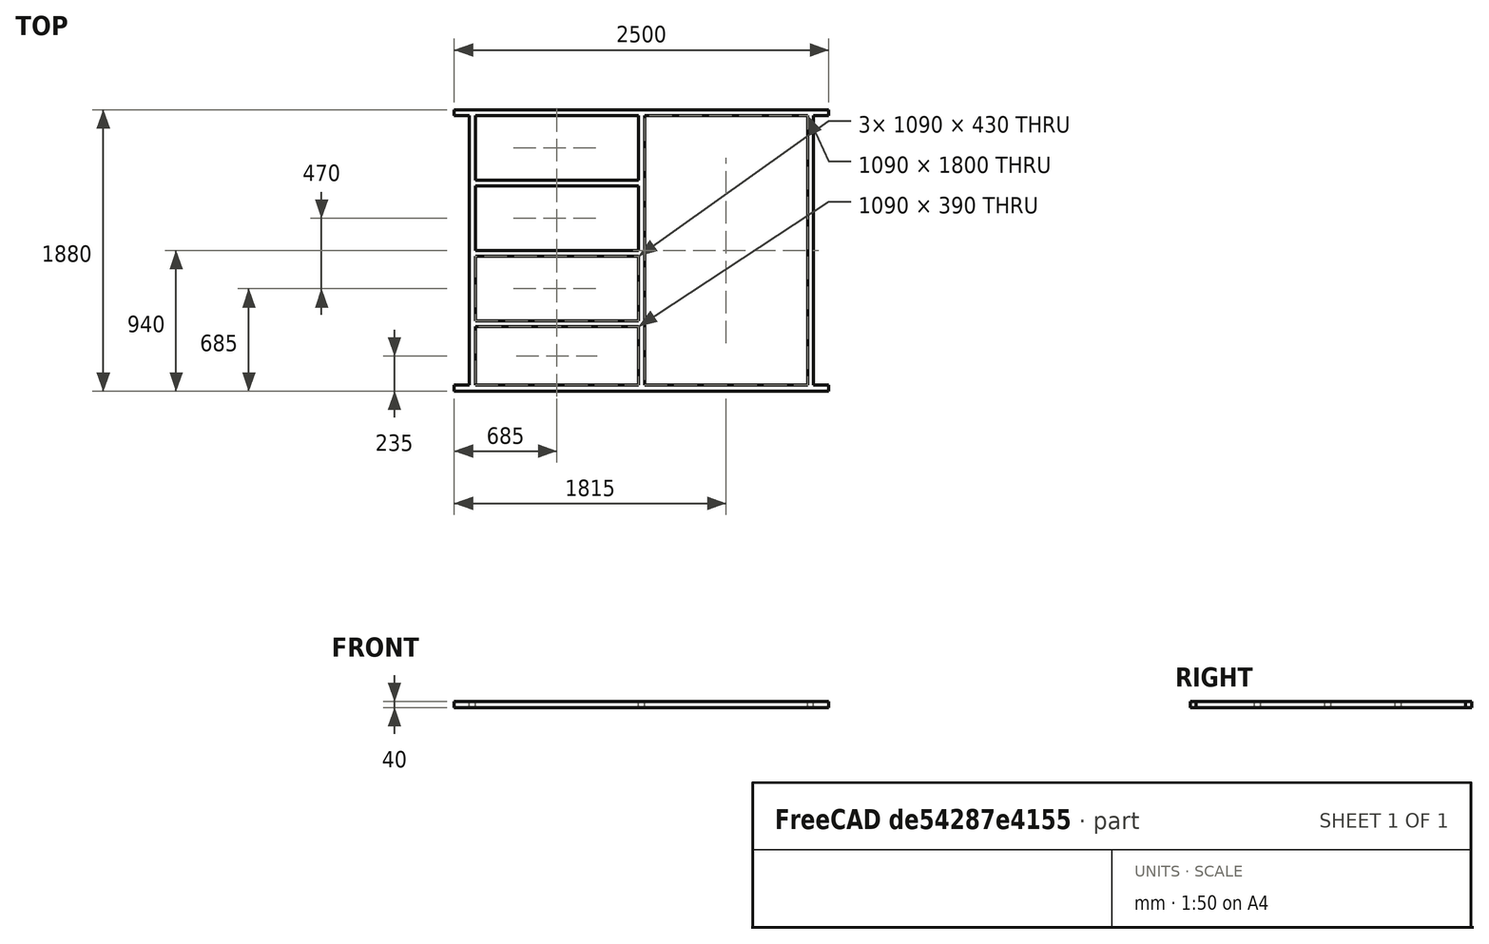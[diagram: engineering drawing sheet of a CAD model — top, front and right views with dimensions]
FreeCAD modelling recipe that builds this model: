
FCSTD DOCUMENT  (FreeCAD 0.19R24291 (Git))
Label: planche jacuzzy
License: All rights reserved
LicenseURL: http://en.wikipedia.org/wiki/All_rights_reserved
objects: Sketcher::SketchObject×1, PartDesign::Pad×1, PartDesign::Body×1
note: 4 computed .brp shape members not serialized (recipe doc carries the construction recipe); baked Part::Feature solids carry a one-line shape summary decoded from their .brp

FEATURE [Sketcher::SketchObject] Sketch
  FullyConstrained = true
  MapMode = 5
  Support = -> [XY_Plane]
  sketch-geometry (32):
    g0: LineSegment StartX=-1250 StartY=940 StartZ=0 EndX=1250 EndY=940 EndZ=0
    g1: LineSegment StartX=1250 StartY=-940 StartZ=0 EndX=-1250 EndY=-940 EndZ=0
    g2: LineSegment StartX=-1250 StartY=900 StartZ=0 EndX=-1150 EndY=900 EndZ=0
    g3: LineSegment StartX=1250 StartY=-900 StartZ=0 EndX=1150 EndY=-900 EndZ=0
    g4: LineSegment StartX=-1250 StartY=940 StartZ=0 EndX=-1250 EndY=900 EndZ=0
    g5: LineSegment StartX=-1250 StartY=-900 StartZ=0 EndX=-1250 EndY=-940 EndZ=0
    g6: LineSegment StartX=1250 StartY=940 StartZ=0 EndX=1250 EndY=900 EndZ=0
    g7: LineSegment StartX=1250 StartY=-900 StartZ=0 EndX=1250 EndY=-940 EndZ=0
    g8: LineSegment StartX=-1150 StartY=900 StartZ=0 EndX=-1150 EndY=-900 EndZ=0
    g9: LineSegment StartX=-1110 StartY=900 StartZ=0 EndX=-1110 EndY=470 EndZ=0
    g10: LineSegment StartX=-1110 StartY=900 StartZ=0 EndX=-20 EndY=900 EndZ=0
    g11: LineSegment StartX=-1150 StartY=-900 StartZ=0 EndX=-1250 EndY=-900 EndZ=0
    g12: LineSegment StartX=1150 StartY=900 StartZ=0 EndX=1150 EndY=-900 EndZ=0
    g13: LineSegment StartX=1110 StartY=900 StartZ=0 EndX=1110 EndY=-900 EndZ=0
    g14: LineSegment StartX=1150 StartY=900 StartZ=0 EndX=1250 EndY=900 EndZ=0
    g15: LineSegment StartX=1110 StartY=-900 StartZ=0 EndX=20 EndY=-900 EndZ=0
    g16: LineSegment StartX=-20 StartY=900 StartZ=0 EndX=-20 EndY=470 EndZ=0
    g17: LineSegment StartX=20 StartY=900 StartZ=0 EndX=20 EndY=-900 EndZ=0
    g18: LineSegment StartX=20 StartY=900 StartZ=0 EndX=1110 EndY=900 EndZ=0
    g19: LineSegment StartX=-20 StartY=-900 StartZ=0 EndX=-1110 EndY=-900 EndZ=0
    g20: LineSegment StartX=-1110 StartY=470 StartZ=0 EndX=-20 EndY=470 EndZ=0
    g21: LineSegment StartX=-1110 StartY=430 StartZ=0 EndX=-20 EndY=430 EndZ=0
    g22: LineSegment StartX=-1110 StartY=-2.842e-13 StartZ=0 EndX=-20 EndY=-2.842e-13 EndZ=0
    g23: LineSegment StartX=-1110 StartY=-40 StartZ=0 EndX=-20 EndY=-40 EndZ=0
    g24: LineSegment StartX=-1110 StartY=-470 StartZ=0 EndX=-20 EndY=-470 EndZ=0
    g25: LineSegment StartX=-1110 StartY=-510 StartZ=0 EndX=-20 EndY=-510 EndZ=0
    g26: LineSegment StartX=-1110 StartY=430 StartZ=0 EndX=-1110 EndY=-2.842e-13 EndZ=0
    g27: LineSegment StartX=-20 StartY=430 StartZ=0 EndX=-20 EndY=-2.842e-13 EndZ=0
    g28: LineSegment StartX=-1110 StartY=-40 StartZ=0 EndX=-1110 EndY=-470 EndZ=0
    g29: LineSegment StartX=-20 StartY=-40 StartZ=0 EndX=-20 EndY=-470 EndZ=0
    g30: LineSegment StartX=-1110 StartY=-510 StartZ=0 EndX=-1110 EndY=-900 EndZ=0
    g31: LineSegment StartX=-20 StartY=-510 StartZ=0 EndX=-20 EndY=-900 EndZ=0
  constraints (88):
    c: Horizontal(g1)
    c: DistanceY(g1,g0) = 1880
    c: DistanceX(g0,g0) = 2500
    c: Symmetric(g0,g1,g-1)
    c: Symmetric(g0,g0,g-2)
    c: Horizontal(g3)
    c: Symmetric(g2,g14,g-2)
    c: Symmetric(g2,g11,g-1)
    c: DistanceY(g2,g0) = 40
    c: Coincident(g4,g0)
    c: Coincident(g4,g2)
    c: Vertical(g4)
    c: Coincident(g5,g11)
    c: Coincident(g5,g1)
    c: Vertical(g5)
    c: Coincident(g6,g0)
    c: Coincident(g6,g14)
    c: Coincident(g7,g3)
    c: Coincident(g7,g1)
    c: Vertical(g7)
    c: Vertical(g8)
    c: DistanceX(g2,g8) = 100
    c: Vertical(g9)
    c: DistanceX(g8,g9) = 40
    c: Coincident(g2,g8)
    c: Coincident(g10,g9)
    c: Tangent(g2,g10)
    c: Coincident(g19,g30)
    c: Coincident(g11,g8)
    c: Tangent(g3,g11)
    c: Vertical(g13)
    c: Vertical(g12)
    c: DistanceX(g13,g12) = 40
    c: DistanceX(g12,g6) = 100
    c: Coincident(g18,g13)
    c: Coincident(g14,g12)
    c: Tangent(g10,g14)
    c: Coincident(g3,g12)
    c: Coincident(g15,g13)
    c: Tangent(g3,g15)
    c: Vertical(g16)
    c: Vertical(g17)
    c: DistanceX(g16,g17) = 40
    c: Symmetric(g16,g17,g-2)
    c: Coincident(g10,g16)
    c: PointOnObject(g18,g17)
    c: Tangent(g10,g18)
    c: Coincident(g15,g17)
    c: Coincident(g19,g31)
    c: Tangent(g15,g19)
    c: Horizontal(g20)
    c: Horizontal(g21)
    c: DistanceY(g21,g20) = 40
    c: Horizontal(g22)
    c: Horizontal(g23)
    c: DistanceY(g23,g22) = 40
    c: PointOnObject(g23,g9)
    c: PointOnObject(g22,g9)
    c: Horizontal(g24)
    c: Horizontal(g25)
    c: DistanceY(g25,g24) = 40
    c: PointOnObject(g25,g9)
    c: PointOnObject(g24,g9)
    c: PointOnObject(g22,g16)
    c: PointOnObject(g23,g16)
    c: PointOnObject(g24,g16)
    c: PointOnObject(g25,g16)
    c: DistanceY(g20,g10) = 430
    c: DistanceY(g22,g21) = 430
    c: DistanceY(g24,g23) = 430
    c: Coincident(g9,g20)
    c: Coincident(g26,g21)
    c: Tangent(g9,g26)
    c: Coincident(g16,g20)
    c: Coincident(g27,g21)
    c: Tangent(g16,g27)
    c: PointOnObject(g26,g22)
    c: PointOnObject(g28,g23)
    c: Tangent(g26,g28)
    c: PointOnObject(g27,g22)
    c: PointOnObject(g29,g23)
    c: Tangent(g27,g29)
    c: PointOnObject(g28,g24)
    c: PointOnObject(g30,g25)
    c: Tangent(g28,g30)
    c: PointOnObject(g29,g24)
    c: PointOnObject(g31,g25)
    c: Tangent(g29,g31)
FEATURE [PartDesign::Pad] Pad
  Direction = (1,1,1)
  Length = 40
  Length2 = 100
  Profile = -> Sketch
  Type = 0
FEATURE [PartDesign::Body] Body
  Group = -> [Sketch,Pad]
  Origin = -> Origin
  Tip = -> Pad
